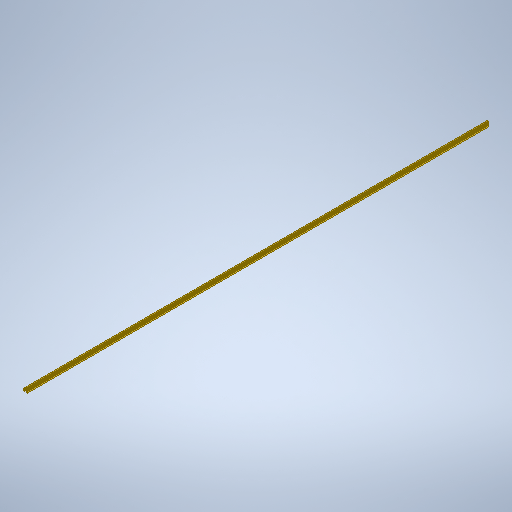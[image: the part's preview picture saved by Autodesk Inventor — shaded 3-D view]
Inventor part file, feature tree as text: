
AUTODESK INVENTOR PART (.ipt)
format: ipt  version: 2025.2 (Build 292293000, 293)  size: 353,792 bytes
history: native  units: mm
features: other x1, extrude x1, sketch x1
ambient origin geometry x8: Origin, YZ Plane, XZ Plane, XY Plane, X Axis, Y Axis, Z Axis, Center Point
bodies: Body1 (feature_tree)
feature tree (3):
  other  "Sólido1"
  extrude  "Extrusão1"  Depth=0.5mm
  sketch  "Esboço2"  dims[d6=5.0mm d7=20.0mm d8=10.0mm d9=6.2mm d11=6.0mm d17=2.0mm d22=0.5mm d24=0.5mm d65=1.5mm d67=1.5mm d69=1.5mm d70=1.5mm d72=1.5mm d75=2000.0mm d76=0.0mm d25=0.872665mm d26=0.5mm d27=0.872665mm]
